# Revit family: QF_BOURGEAT_Satellite4G_GN6_pied_inox_chaud
name_source: partatom
category: Equipement spécialisé
revit_build: Autodesk Revit 2015 (Build: 20140606_1530(x64)
units: mm (PartAtom-declared; Revit-internal decimal feet)

## types (8) — shared parameters
Certification = NF hygiene alimentaire
Charge max = 60.00 kg
Diametre_roue = 80 mm  [stored 0.262467 ft]
Fabricant = BOURGEAT
Fréquence = 50 Hz
Hauteur_poignee_porte_sol = 241 mm  [stored 0.790682 ft]
Hauteur_poignees_laterales = 804 mm  [stored 2.6378 ft]
Indice de protection = IP25
Intensité nominale = 4 A
Materiau_Poignee_porte = B_Elastomère_TPE_S
Materiau_bac = Acier inoxydable, brossé
Materiau_bandage = B_Elastomère_TPE_S
Materiau_porte = Acier inoxydable, brossé
Materiau_vitre = Verre, vitrage transparent, trempé
Nature isolant = Mousse sans PU
Phase = 2
Poids net à vide = 50.00 kg
Pos_V_IHM = 38 mm  [stored 0.124672 ft]
Puissance électrique  = 950 W
Spécification du Fabricant = Satellite 4G
Tension = 230 V
URL catalogue = http://www.bourgeat.fr

## per-type parameters (varying)
| type | Consommation énergétique | Hauteur hors tout | Hauteur_pied_inox | Hauteur_porte | Humidification | Largeur_porte | Longueur hors tout | Longueur_poignees_laterales | Modèle | Poignee_droite | Poignee_gauche | Profondeur hors tout |
| GN6_1/1_entrree530_humidification_porte_inox_tirant_gauche | 0.27Kwh/h NFD40-016 | 732 mm | 153 mm  [stored 0.501969 ft] | 539 mm | Oui | 706 mm  [stored 2.31627 ft] | 752 mm  [stored 2.46719 ft] | 609 mm  [stored 1.99803 ft] | 840306 + 844017 + 844018 | Non | Oui | 765 mm  [stored 2.50984 ft] |
| GN6_1/1_entrree530_humidification_porte_inox_tirant_droit | 0.27Kwh/h NFD40-016 | 732 mm | 154 mm | 539 mm | Oui | 706 mm  [stored 2.31627 ft] | 752 mm  [stored 2.46719 ft] | 609 mm  [stored 1.99803 ft] | 840306 + 844000 + 844017 + 844018 | Oui | Non | 765 mm  [stored 2.50984 ft] |
| GN6_1/1_entrree530_sans_humidification_porte_inox_tirant_droit | 0.27Kwh/h NFD40-016 | 732 mm | 153 mm  [stored 0.501969 ft] | 539 mm | Non | 706 mm  [stored 2.31627 ft] | 752 mm  [stored 2.46719 ft] | 609 mm  [stored 1.99803 ft] | 840206 + 844000 + 844017 | Oui | Non | 765 mm  [stored 2.50984 ft] |
| GN6_1/1_entrree530_sans_humidification_porte_inox_tirant_gauche | 0.27Kwh/h NFD40-016 | 732 mm | 154 mm | 539 mm | Non | 706 mm  [stored 2.31627 ft] | 752 mm  [stored 2.46719 ft] | 609 mm  [stored 1.99803 ft] | 840206 + 844017 | Non | Oui | 765 mm  [stored 2.50984 ft] |
| GN6_1/1_entrree325_humidification_porte_inox_tirant_droit | 0.24Kwh/h NFD40-016 | 695 mm  [stored 2.28018 ft] | 153 mm  [stored 0.501969 ft] | 502 mm  [stored 1.64698 ft] | Oui | 501 mm | 547 mm | 665 mm  [stored 2.18176 ft] | 843306 + 844000 + 844017 +844018 | Oui | Non | 821 mm  [stored 2.69357 ft] |
| GN6_1/1_entrree325_humidification_porte_inox_tirant_gauche | 0.24Kwh/h NFD40-016 | 695 mm  [stored 2.28018 ft] | 153 mm  [stored 0.501969 ft] | 502 mm  [stored 1.64698 ft] | Oui | 501 mm | 547 mm | 665 mm  [stored 2.18176 ft] | 843306 + 844017 + 844018 | Non | Oui | 821 mm  [stored 2.69357 ft] |
| GN6_1/1_entrree325_sans_humidification_porte_inox_tirant_gauche | 0.24Kwh/h NFD40-016 | 695 mm  [stored 2.28018 ft] | 154 mm | 502 mm  [stored 1.64698 ft] | Non | 501 mm | 547 mm | 665 mm  [stored 2.18176 ft] | 843206 + 844017 | Non | Oui | 821 mm  [stored 2.69357 ft] |
| GN6_1/1_entrree325_sans_humidification_porte_inox_tirant_droit | 0.24Kwh/h NFD40-016 | 695 mm  [stored 2.28018 ft] | 153 mm  [stored 0.501969 ft] | 502 mm  [stored 1.64698 ft] | Non | 501 mm | 547 mm | 665 mm  [stored 2.18176 ft] | 843206 + 844000 + 844017 | Oui | Non | 821 mm  [stored 2.69357 ft] |

note: [stored X ft] marks values corroborated as IEEE doubles in the binary element streams (Revit-internal decimal feet)
